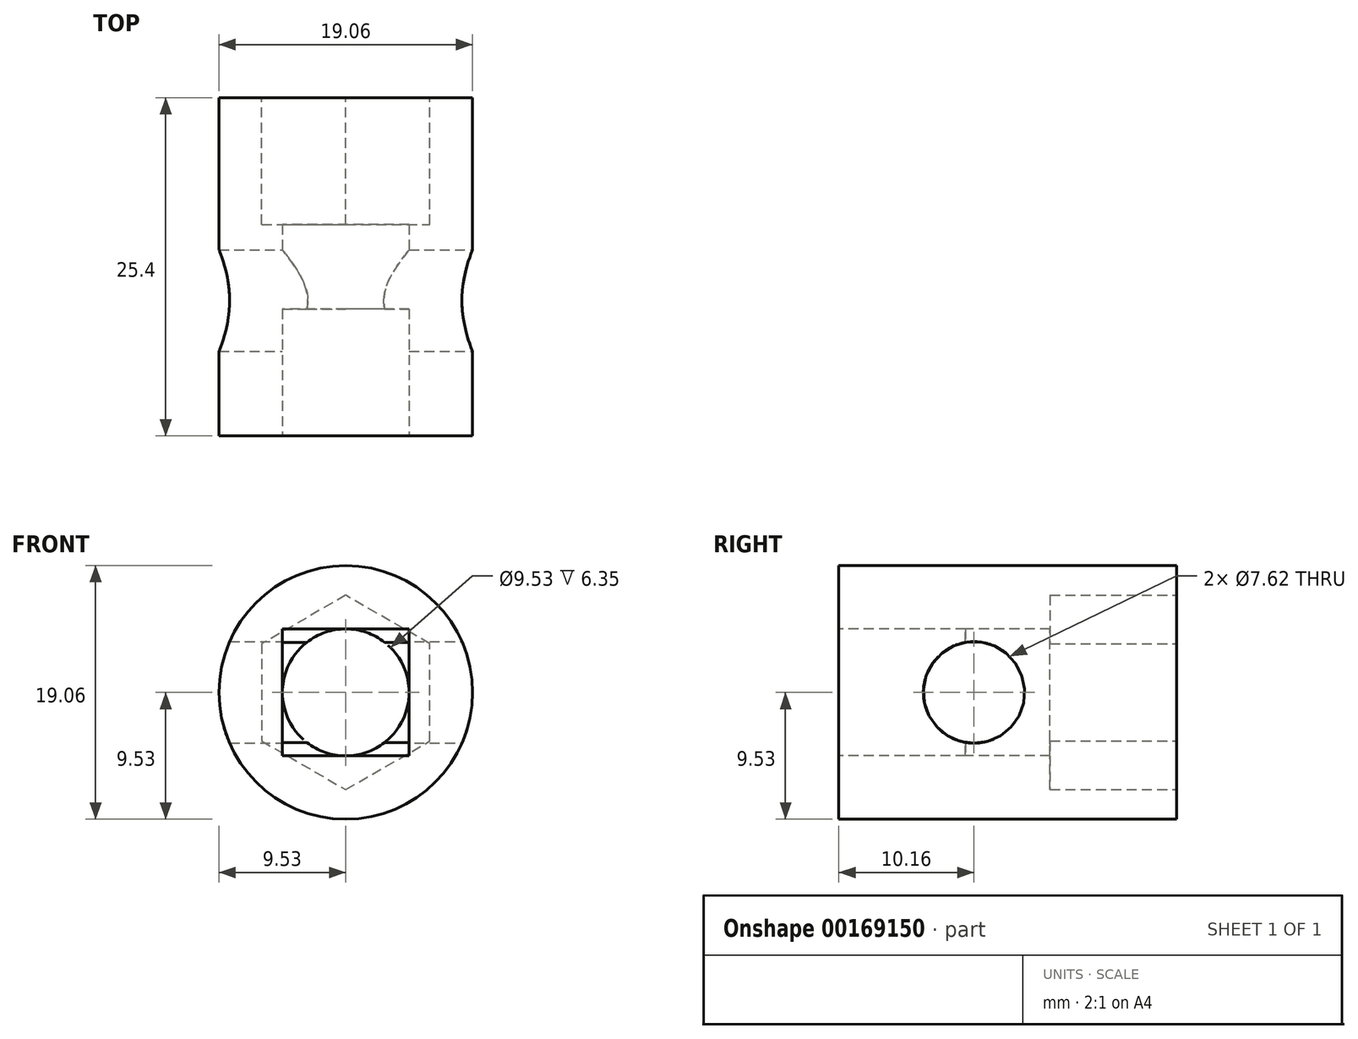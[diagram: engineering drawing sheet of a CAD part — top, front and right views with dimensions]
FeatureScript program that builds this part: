
annotation { "Feature Type Name" : "Feature", "Feature Type Description" : "" }
export const myFeature = defineFeature(function(context is Context, id is Id, definition is map)
    precondition{}
    {
        {
            var Q0;
            Q0=qCreatedBy(makeId("Front.planeOp"),FACE);
            var sketch = newSketch(context, id + "F0", { "sketchPlane" : qUnion([Q0])});
            skCircle(sketch, "E0", {"center": v(0, 0) * mm, "radius": 9.53 * mm});
            skSolve(sketch);
        }
        {
            var Q0;
            Q0 = qSketchRegion(id + "F0", true);
            extrude(context, id + "F1", {"entities" : qUnion([Q0]), "oppositeDirection" : true, "depth" : 25.4 * mm});
        }
        {
            var Q0;
            Q0=makeQuery(id+"F1.opExtrude","CAP_FACE",FACE,{"disambiguationData":[OSD([sQuery(id+"F0.wireOp",EDGE,"E0")])],"isStart":true});
            var sketch = newSketch(context, id + "F2", { "sketchPlane" : qUnion([Q0])});
            skLineSegment(sketch, "E1.bottom", {"start": v(4.76, 4.76) * mm, "end": v(-4.76, 4.76) * mm});
            skLineSegment(sketch, "E1.top", {"start": v(4.76, -4.76) * mm, "end": v(-4.76, -4.76) * mm});
            skLineSegment(sketch, "E1.left", {"start": v(4.76, 4.76) * mm, "end": v(4.76, -4.76) * mm});
            skLineSegment(sketch, "E1.right", {"start": v(-4.76, 4.76) * mm, "end": v(-4.76, -4.76) * mm});
            skCircle(sketch, "E2", {"center": v(0, 0) * mm, "radius": 4.76 * mm});
            skSolve(sketch);
        }
        {
            var Q0;
            {var subQ0=sQuery(id+"F2.wireOp",EDGE,"E2");var subQ1=makeQuery(id+"F2.imprint","INTERSECT",VERTEX,{"derivedFrom":[sQuery(id+"F2.wireOp",EDGE,"E1.bottom"),subQ0]});Q0=makeQuery(id+"F2.imprint","IMPRINT",FACE,{"disambiguationData":[TD([[makeQuery(id+"F2.imprint","IMPRINT",EDGE,{"disambiguationData":[TD([[subQ1,1.0]])],"derivedFrom":subQ0}),1.0]])]});}
            extrude(context, id + "F3", {"entities" : qUnion([Q0]), "operationType" : NewBodyOperationType.REMOVE, "endBound" : BoundingType.THROUGH_ALL, "oppositeDirection" : true, "depth" : 25.4 * mm});
        }
        {
            var Q0;
            Q0 = qSketchRegion(id + "F2", true);
            extrude(context, id + "F4", {"entities" : qUnion([Q0]), "operationType" : NewBodyOperationType.REMOVE, "oppositeDirection" : true, "depth" : 9.52 * mm});
        }
        {
            var Q0;
            Q0=makeQuery(id+"F1.opExtrude","CAP_FACE",FACE,{"disambiguationData":[OSD([sQuery(id+"F0.wireOp",EDGE,"E0")])],"isStart":false});
            var sketch = newSketch(context, id + "F5", { "sketchPlane" : qUnion([Q0])});
            skCircle(sketch, "E3.cCircle", {"center": v(0, 0) * mm, "radius": 6.32 * mm, "construction": true});
            skLineSegment(sketch, "E3.0", {"start": v(-6.32, -3.65) * mm, "end": v(-6.32, 3.65) * mm});
            skLineSegment(sketch, "E3.1", {"start": v(-6.32, 3.65) * mm, "end": v(0, 7.3) * mm});
            skLineSegment(sketch, "E3.2", {"start": v(0, 7.3) * mm, "end": v(6.32, 3.65) * mm});
            skLineSegment(sketch, "E3.3", {"start": v(6.32, 3.65) * mm, "end": v(6.32, -3.65) * mm});
            skLineSegment(sketch, "E3.4", {"start": v(6.32, -3.65) * mm, "end": v(0, -7.3) * mm});
            skLineSegment(sketch, "E3.5", {"start": v(0, -7.3) * mm, "end": v(-6.32, -3.65) * mm});
            skPoint(sketch, "E3.0.midPoint", {"position": v(-6.32, 0) * mm});
            skSolve(sketch);
        }
        {
            var Q0;
            Q0=makeQuery(id+"F5.imprint","IMPRINT",FACE,{"disambiguationData":[TD([[makeQuery(id+"F5.imprint","IMPRINT",EDGE,{"derivedFrom":sQuery(id+"F5.wireOp",EDGE,"E3.0")}),-1.0]])]});
            extrude(context, id + "F6", {"entities" : qUnion([Q0]), "operationType" : NewBodyOperationType.REMOVE, "oppositeDirection" : true, "depth" : 9.52 * mm});
        }
        {
            var Q0;
            Q0=qCreatedBy(makeId("Right.planeOp"),FACE);
            var sketch = newSketch(context, id + "F7", { "sketchPlane" : qUnion([Q0])});
            skCircle(sketch, "E4", {"center": v(10.16, 0) * mm, "radius": 3.81 * mm});
            skSolve(sketch);
        }
        {
            var Q0;
            Q0 = qSketchRegion(id + "F7", true);
            extrude(context, id + "F8", {"entities" : qUnion([Q0]), "operationType" : NewBodyOperationType.REMOVE, "endBound" : BoundingType.SYMMETRIC, "oppositeDirection" : true, "depth" : 25.4 * mm});
        }
    });
